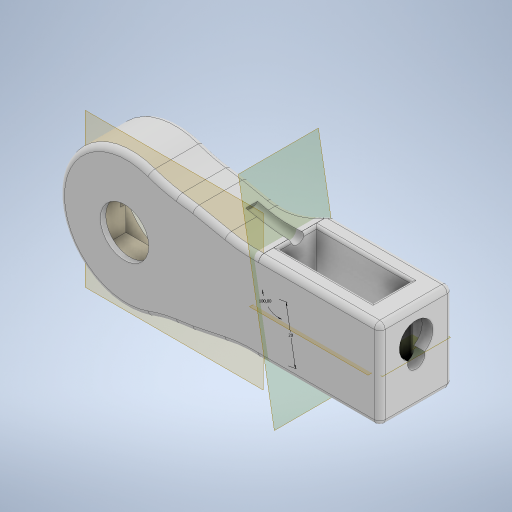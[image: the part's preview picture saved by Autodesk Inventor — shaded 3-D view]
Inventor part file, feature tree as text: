
AUTODESK INVENTOR PART (.ipt)
format: ipt  version: 2024 (Build 280153000, 153)  size: 2,944,000 bytes
history: native  units: mm
features: extrude x13, projected_geometry x9, plane x6, fillet x6, other x6, mirror x3, reference x3
ambient origin geometry x8: Origin, YZ Plane, XZ Plane, XY Plane, X Axis, Y Axis, Z Axis, Center Point
bodies: Solid1 (feature_tree)
feature tree (46):
  plane  "Work Plane1"
  extrude  "Extrusion1"  Depth=40.25mm
  extrude  "Extrusion2"  Depth=20.25mm
  plane  "Work Plane2"
  extrude  "Extrusion3"  TaperAngle=0.0deg  [1 undecoded]
  mirror  "Mirror2"
  extrude  "Extrusion4"  Depth=40.25mm
  extrude  "Extrusion6"  Depth=50.0mm
  fillet  "Fillet1"  Radius=49.05mm
  extrude  "Extrusion7"  Depth=15.0mm
  extrude  "Extrusion8"  Depth=15.0mm
  extrude  "Extrusion9"  Depth=20.0mm
  extrude  "Extrusion10"  Depth=20.0mm
  plane  "Work Plane3"
  fillet  "Fillet7"  Radius=12.817996mm
  fillet  "Fillet8"  Radius=12.817996mm
  fillet  "Fillet10"  Radius=8.0mm
  extrude  "Extrusion12"  Depth=10.125mm
  fillet  "Fillet15"  Radius=5.5mm
  extrude  "Extrusion13"  Depth=1.0mm
  fillet  "Fillet16"  Radius=1.0mm
  extrude  "Extrusion15"  Depth=2.0mm TaperAngle=0.0deg
  plane  "Work Plane7"
  extrude  "Extrusion17"  Depth=20.5mm
  plane  "Work Plane8"
  mirror  "Mirror4"
  plane  "Work Plane9"
  mirror  "Mirror5"
  reference  "Reference1"
  reference  "Reference2"
  reference  "Reference3"
  projected_geometry  "Projected Loop1"
  projected_geometry  "Projected Loop2"
  projected_geometry  "Projected Loop3"
  projected_geometry  "Projected Loop5"
  projected_geometry  "Projected Loop7"
  projected_geometry  "Projected Loop8"
  projected_geometry  "Projected Loop10"
  projected_geometry  "Projected Loop12"
  projected_geometry  "Projected Loop14"
  other  "<userpath> windows\Documents\Inventor\Robotska_roka\Assembly4.iam"
  other  "Assembly4.iam"
  other  "Servo Motor MG996R  With Attachments:5"
  other  "servoMotorMG996R_7"
  other  "Servo Motor MG996R  With Attachments:6"
  other  "attachmentCircular_1"
note: 1 required parameter value undecoded (feature->parameter linkage not recoverable at this tier; creation-order binding heuristic only, values carry confidence <= 0.55)
